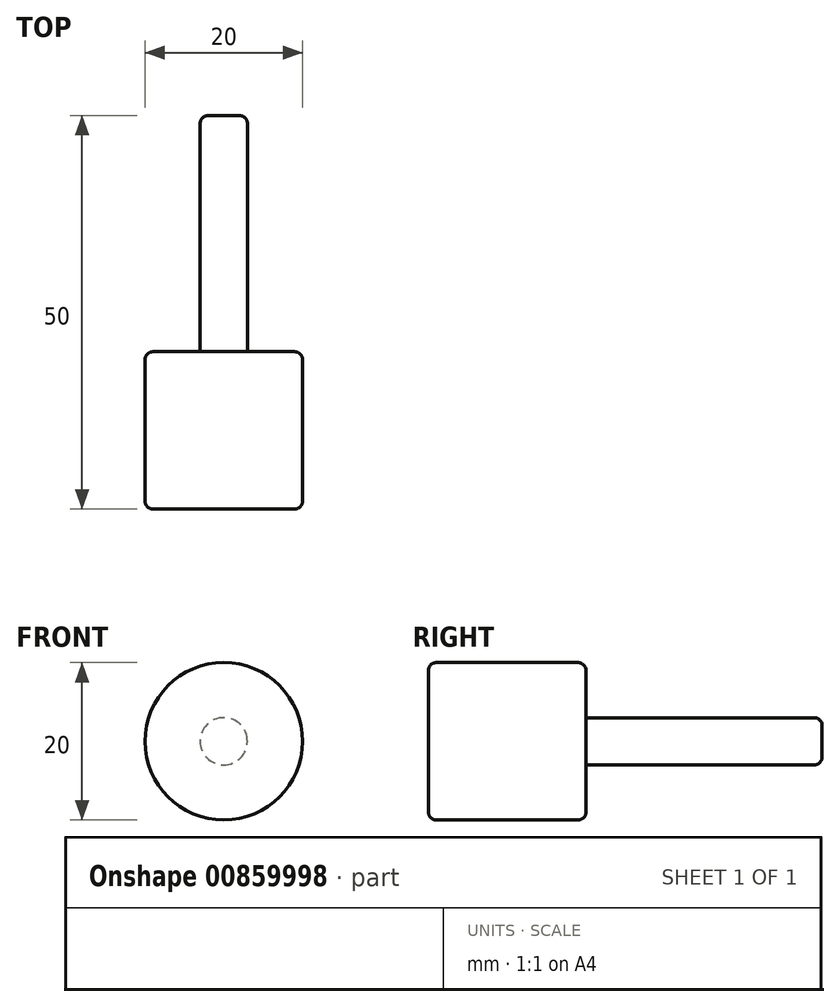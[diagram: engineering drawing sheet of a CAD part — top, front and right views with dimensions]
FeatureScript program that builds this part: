
annotation { "Feature Type Name" : "Feature", "Feature Type Description" : "" }
export const myFeature = defineFeature(function(context is Context, id is Id, definition is map)
    precondition{}
    {
        {
            var Q0;
            Q0=qCreatedBy(makeId("Front.planeOp"),FACE);
            var sketch = newSketch(context, id + "F0", { "sketchPlane" : qUnion([Q0])});
            skCircle(sketch, "E0", {"center": v(0, 0) * mm, "radius": 3 * mm});
            skSolve(sketch);
        }
        {
            var Q0;
            Q0=makeQuery(id+"F0.imprint","IMPRINT",FACE,{"disambiguationData":[TD([[makeQuery(id+"F0.imprint","IMPRINT",EDGE,{"derivedFrom":sQuery(id+"F0.wireOp",EDGE,"E0")}),1.0]])]});
            extrude(context, id + "F1", {"entities" : qUnion([Q0]), "depth" : 50 * mm, "offsetDistance" : 25 * mm});
        }
        {
            var Q0;
            Q0=makeQuery(id+"F1.opExtrude","CAP_EDGE",EDGE,{"disambiguationData":[OSD([sQuery(id+"F0.wireOp",EDGE,"E0")])],"isStart":true});
            fillet(context, id + "F2", {"entities" : qUnion([Q0]), "radius" : 1 * mm, "tangentPropagation" : true, "allowEdgeOverflow" : false});
        }
        {
            var Q0;
            Q0=makeQuery(id+"F1.opExtrude","CAP_FACE",FACE,{"disambiguationData":[OSD([sQuery(id+"F0.wireOp",EDGE,"E0")])],"isStart":false});
            var sketch = newSketch(context, id + "F3", { "sketchPlane" : qUnion([Q0])});
            skCircle(sketch, "E1", {"center": v(0, 0) * mm, "radius": 10 * mm});
            skSolve(sketch);
        }
        {
            var Q0;
            Q0=makeQuery(id+"F3.imprint","IMPRINT",FACE,{"disambiguationData":[TD([[makeQuery(id+"F3.imprint","IMPRINT",EDGE,{"derivedFrom":sQuery(id+"F3.wireOp",EDGE,"E1")}),1.0]])]});
            var Q1;
            Q1=sQuery(id+"F3.wireOp",EDGE,"E1");
            extrude(context, id + "F4", {"entities" : qUnion([Q0]), "operationType" : NewBodyOperationType.ADD, "surfaceOperationType" : NewSurfaceOperationType.ADD, "surfaceEntities" : qUnion([Q1]), "oppositeDirection" : true, "depth" : 20 * mm, "offsetDistance" : 25 * mm});
        }
        {
            var Q0;
            Q0=makeQuery(id+"F4.opExtrude","CAP_EDGE",EDGE,{"disambiguationData":[OSD([sQuery(id+"F0.wireOp",EDGE,"E0")])],"isStart":false});
            var Q1;
            Q1=makeQuery(id+"F4.opExtrude","CAP_EDGE",EDGE,{"disambiguationData":[OSD([sQuery(id+"F3.wireOp",EDGE,"E1")])],"isStart":false});
            var Q2;
            Q2=makeQuery(id+"F4.opExtrude","CAP_EDGE",EDGE,{"disambiguationData":[OSD([sQuery(id+"F3.wireOp",EDGE,"E1")])],"isStart":true});
            fillet(context, id + "F5", {"entities" : qUnion([Q0, Q1, Q2]), "radius" : 1 * mm, "tangentPropagation" : true, "allowEdgeOverflow" : false});
        }
    });
